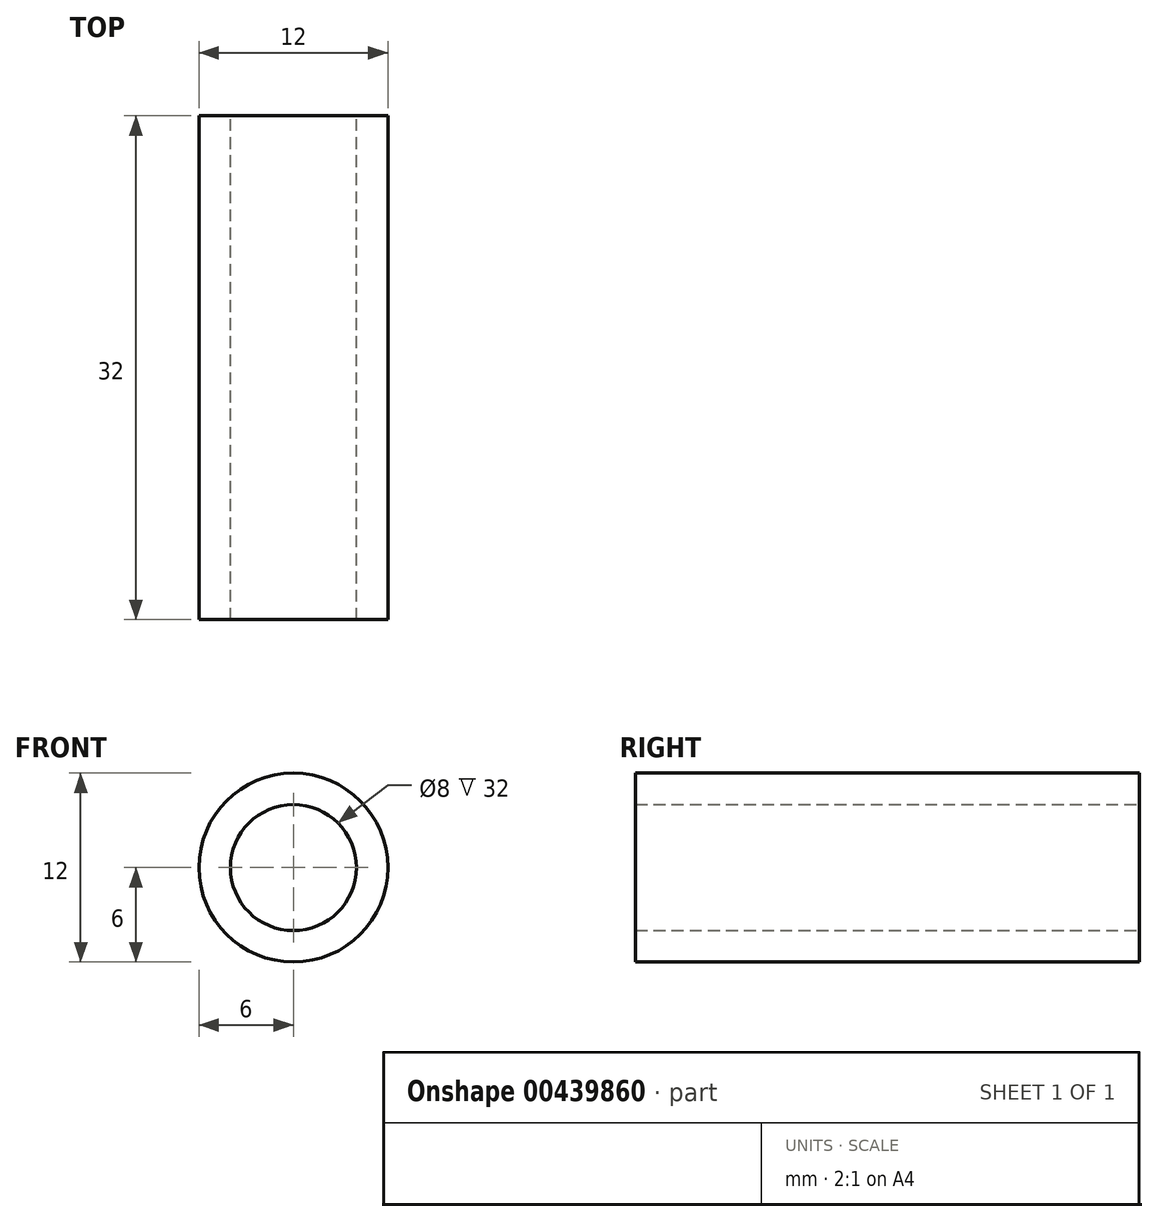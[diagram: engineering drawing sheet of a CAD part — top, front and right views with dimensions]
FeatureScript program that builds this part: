
annotation { "Feature Type Name" : "Feature", "Feature Type Description" : "" }
export const myFeature = defineFeature(function(context is Context, id is Id, definition is map)
    precondition{}
    {
        {
            assignVariable(context, id + "F0", {"name" : "x3", "anyValue" : 32});
        }
        {
            var Q0;
            Q0=qCreatedBy(makeId("Front.planeOp"),FACE);
            var sketch = newSketch(context, id + "F1", { "sketchPlane" : qUnion([Q0])});
            skCircle(sketch, "E0", {"center": v(0, 0) * mm, "radius": 6 * mm});
            skCircle(sketch, "E1", {"center": v(0, 0) * mm, "radius": 4 * mm});
            skSolve(sketch);
        }
        {
            var Q0;
            Q0 = qSketchRegion(id + "F1", true);
            extrude(context, id + "F2", {"entities" : qUnion([Q0]), "depth" : (getVariable(context, 'x3')) * mm});
        }
    });
